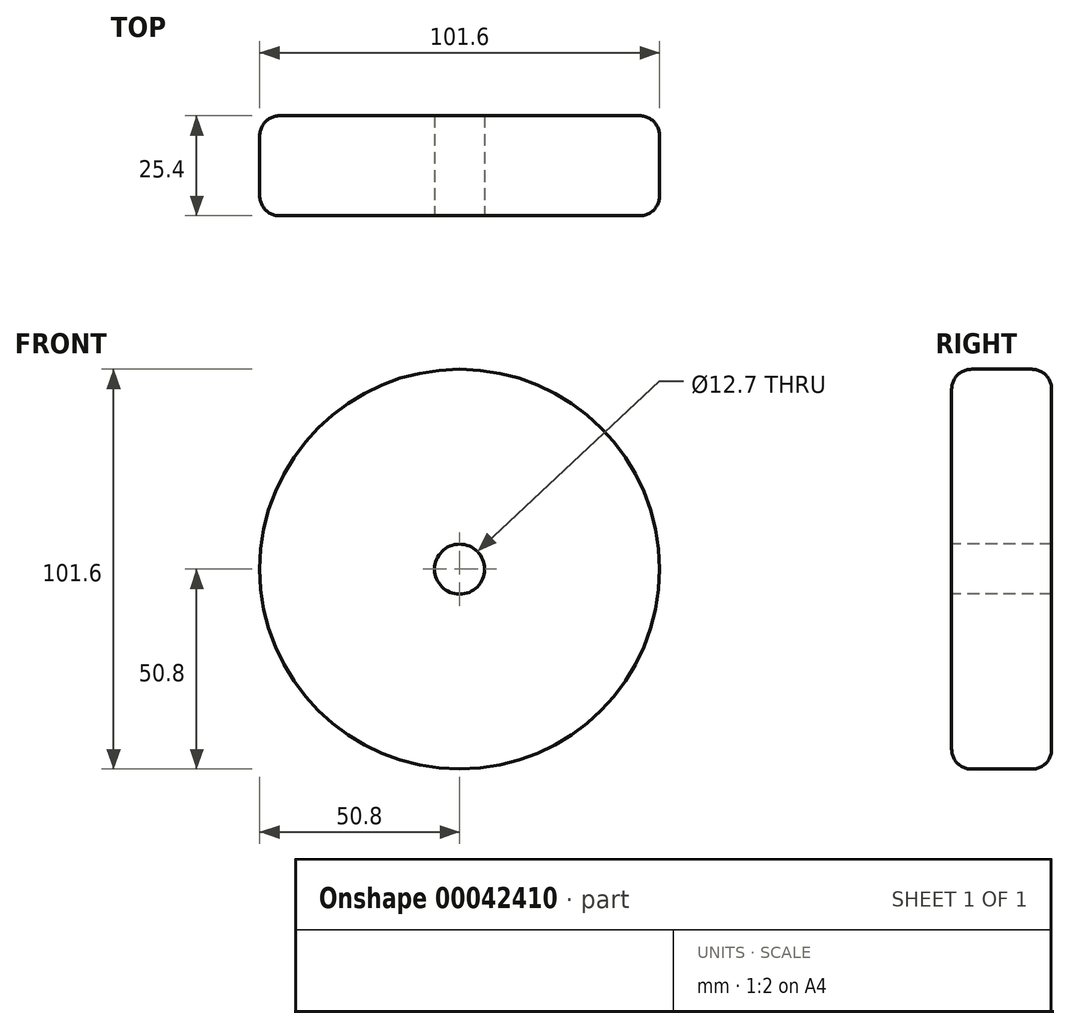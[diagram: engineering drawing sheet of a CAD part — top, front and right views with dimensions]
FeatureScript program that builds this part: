
annotation { "Feature Type Name" : "Feature", "Feature Type Description" : "" }
export const myFeature = defineFeature(function(context is Context, id is Id, definition is map)
    precondition{}
    {
        {
            var Q0;
            Q0=qCreatedBy(makeId("Front.planeOp"),FACE);
            var sketch = newSketch(context, id + "F0", { "sketchPlane" : qUnion([Q0])});
            skCircle(sketch, "E0", {"center": v(0, 0) * mm, "radius": 50.8 * mm});
            skSolve(sketch);
        }
        {
            var Q0;
            Q0=makeQuery(id+"F0.imprint","IMPRINT",FACE,{"disambiguationData":[TD([[makeQuery(id+"F0.imprint","IMPRINT",EDGE,{"derivedFrom":sQuery(id+"F0.wireOp",EDGE,"E0")}),1.0]])]});
            extrude(context, id + "F1", {"entities" : qUnion([Q0]), "depth" : 25.4 * mm});
        }
        {
            var Q0;
            Q0=makeQuery(id+"F1.opExtrude","CAP_EDGE",EDGE,{"disambiguationData":[OSD([sQuery(id+"F0.wireOp",EDGE,"E0")])],"isStart":false});
            var Q1;
            Q1=makeQuery(id+"F1.opExtrude","CAP_EDGE",EDGE,{"disambiguationData":[OSD([sQuery(id+"F0.wireOp",EDGE,"E0")])],"isStart":true});
            fillet(context, id + "F2", {"entities" : qUnion([Q0, Q1]), "radius" : 5.08 * mm, "tangentPropagation" : true, "allowEdgeOverflow" : false});
        }
        {
            var Q0;
            Q0=makeQuery(id+"F1.opExtrude","CAP_FACE",FACE,{"disambiguationData":[OSD([sQuery(id+"F0.wireOp",EDGE,"E0")])],"isStart":false});
            var sketch = newSketch(context, id + "F3", { "sketchPlane" : qUnion([Q0])});
            skCircle(sketch, "E1", {"center": v(0, 0) * mm, "radius": 6.35 * mm});
            skSolve(sketch);
        }
        {
            var Q0;
            Q0 = qSketchRegion(id + "F3", true);
            extrude(context, id + "F4", {"entities" : qUnion([Q0]), "operationType" : NewBodyOperationType.REMOVE, "endBound" : BoundingType.THROUGH_ALL, "oppositeDirection" : true, "depth" : 25.4 * mm});
        }
    });
